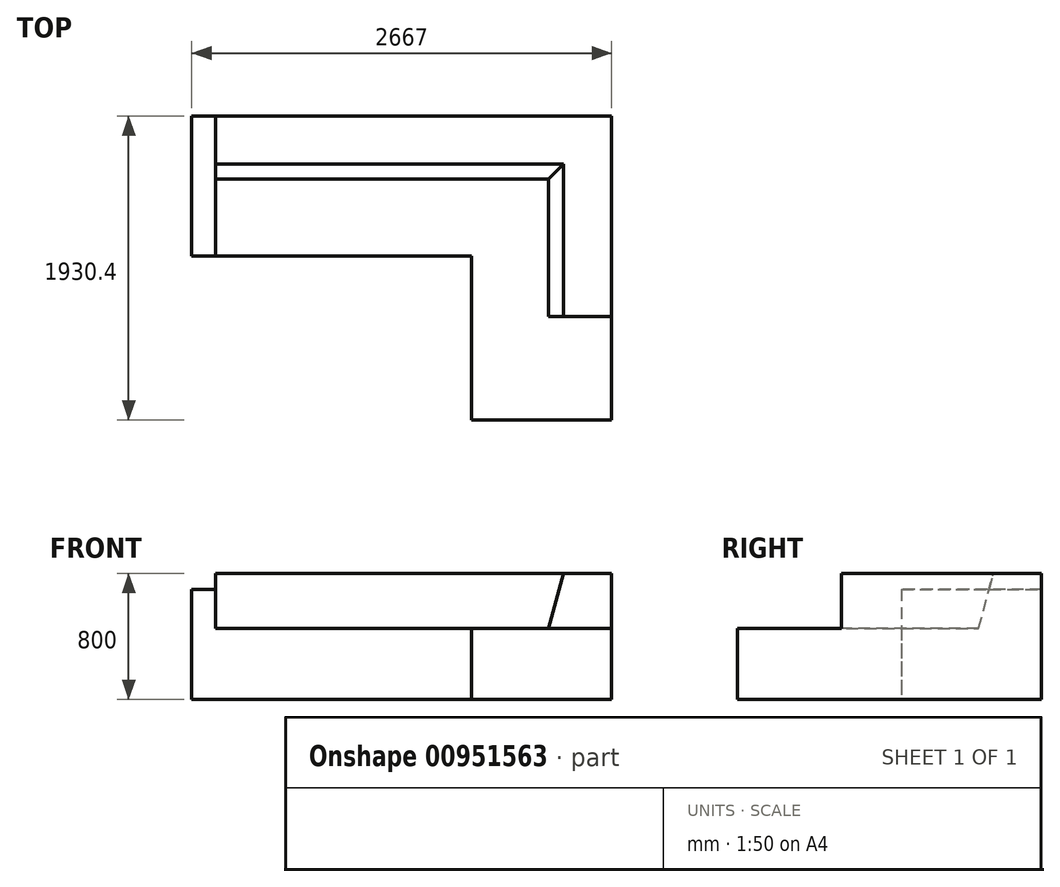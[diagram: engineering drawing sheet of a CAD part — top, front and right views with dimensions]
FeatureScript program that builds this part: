
annotation { "Feature Type Name" : "Feature", "Feature Type Description" : "" }
export const myFeature = defineFeature(function(context is Context, id is Id, definition is map)
    precondition{}
    {
        {
            var Q0;
            Q0=qCreatedBy(makeId("Top.planeOp"),FACE);
            var sketch = newSketch(context, id + "F0", { "sketchPlane" : qUnion([Q0])});
            skLineSegment(sketch, "E0", {"start": v(0, 0) * mm, "end": v(0, 1930.4) * mm});
            skLineSegment(sketch, "E1", {"start": v(0, 1930.4) * mm, "end": v(2667, 1930.4) * mm});
            skLineSegment(sketch, "E2", {"start": v(0, 0) * mm, "end": v(889, 0) * mm});
            skLineSegment(sketch, "E3", {"start": v(2667, 1930.4) * mm, "end": v(2667, 1041.4) * mm});
            skLineSegment(sketch, "E4", {"start": v(889, 0) * mm, "end": v(889, 1041.4) * mm});
            skLineSegment(sketch, "E5", {"start": v(889, 1041.4) * mm, "end": v(2667, 1041.4) * mm});
            skSolve(sketch);
        }
        {
            var Q0;
            Q0=qSketchRegion(id+"F0",true);
            extrude(context, id + "F1", {"entities" : qUnion([Q0]), "depth" : 450 * mm, "offsetDistance" : 25.4 * mm});
        }
        {
            var Q0;
            Q0=makeQuery(id+"F1.opExtrude","CAP_FACE",FACE,{"disambiguationData":[OSD([sQuery(id+"F0.wireOp",EDGE,"E0"),sQuery(id+"F0.wireOp",EDGE,"E1"),sQuery(id+"F0.wireOp",EDGE,"E2"),sQuery(id+"F0.wireOp",EDGE,"E3"),sQuery(id+"F0.wireOp",EDGE,"E4"),sQuery(id+"F0.wireOp",EDGE,"E5")])],"isStart":false});
            var sketch = newSketch(context, id + "F2", { "sketchPlane" : qUnion([Q0])});
            skLineSegment(sketch, "E6.bottom", {"start": v(889, 0) * mm, "end": v(0, 0) * mm});
            skLineSegment(sketch, "E6.top", {"start": v(889, 150) * mm, "end": v(0, 150) * mm});
            skLineSegment(sketch, "E6.left", {"start": v(889, 0) * mm, "end": v(889, 150) * mm});
            skLineSegment(sketch, "E6.right", {"start": v(0, 0) * mm, "end": v(0, 150) * mm});
            skLineSegment(sketch, "E7.bottom", {"start": v(2667, 1041.4) * mm, "end": v(2517, 1041.4) * mm});
            skLineSegment(sketch, "E7.top", {"start": v(2667, 1930.4) * mm, "end": v(2517, 1930.4) * mm});
            skLineSegment(sketch, "E7.left", {"start": v(2667, 1041.4) * mm, "end": v(2667, 1930.4) * mm});
            skLineSegment(sketch, "E7.right", {"start": v(2517, 1041.4) * mm, "end": v(2517, 1930.4) * mm});
            skSolve(sketch);
        }
        {
            var Q0;
            Q0=qSketchRegion(id+"F2",true);
            extrude(context, id + "F3", {"entities" : qUnion([Q0]), "operationType" : NewBodyOperationType.ADD, "depth" : 700 * mm - 450 * mm, "offsetDistance" : 25.4 * mm});
        }
        {
            var Q0;
            Q0=makeQuery(id+"F3.opExtrude","SWEPT_FACE",FACE,{"disambiguationData":[OSD([sQuery(id+"F2.wireOp",EDGE,"E6.top")])]});
            var sketch = newSketch(context, id + "F4", { "sketchPlane" : qUnion([Q0])});
            skLineSegment(sketch, "E8", {"start": v(0, 450) * mm, "end": v(0, 800) * mm});
            skLineSegment(sketch, "E9", {"start": v(0, 800) * mm, "end": v(-306.27, 800) * mm});
            skLineSegment(sketch, "E10", {"start": v(-306.27, 800) * mm, "end": v(-400.05, 450) * mm});
            skLineSegment(sketch, "E11", {"start": v(-400.05, 450) * mm, "end": v(0, 450) * mm});
            skSolve(sketch);
        }
        {
            var Q0;
            Q0=qSketchRegion(id+"F4",true);
            var Q1;
            Q1=makeQuery(id+"F3.boolean.opBoolean","MERGE",FACE,{"derivedFrom":[makeQuery(id+"F1.opExtrude","SWEPT_FACE",FACE,{"disambiguationData":[OSD([sQuery(id+"F0.wireOp",EDGE,"E1")])]}),makeQuery(id+"F3.opExtrude","SWEPT_FACE",FACE,{"disambiguationData":[OSD([sQuery(id+"F2.wireOp",EDGE,"E7.top")])]})]});
            extrude(context, id + "F5", {"entities" : qUnion([Q0]), "operationType" : NewBodyOperationType.ADD, "endBound" : BoundingType.UP_TO_SURFACE, "depth" : 25.4 * mm, "endBoundEntityFace" : qUnion([Q1]), "offsetDistance" : 25.4 * mm});
        }
        {
            var Q0;
            Q0=makeQuery(id+"F3.opExtrude","SWEPT_FACE",FACE,{"disambiguationData":[OSD([sQuery(id+"F2.wireOp",EDGE,"E7.right")])]});
            var sketch = newSketch(context, id + "F6", { "sketchPlane" : qUnion([Q0])});
            skLineSegment(sketch, "E12", {"start": v(-1930.4, 450) * mm, "end": v(-1530.35, 450) * mm});
            skLineSegment(sketch, "E13", {"start": v(-1530.35, 450) * mm, "end": v(-1624.13, 800) * mm});
            skLineSegment(sketch, "E14", {"start": v(-1624.13, 800) * mm, "end": v(-1930.4, 800) * mm});
            skLineSegment(sketch, "E15", {"start": v(-1930.4, 800) * mm, "end": v(-1930.4, 450) * mm});
            skSolve(sketch);
        }
        {
            var Q0;
            Q0=qSketchRegion(id+"F6",true);
            extrude(context, id + "F7", {"entities" : qUnion([Q0]), "operationType" : NewBodyOperationType.ADD, "endBound" : BoundingType.UP_TO_NEXT, "depth" : 25.4 * mm, "offsetDistance" : 25.4 * mm});
        }
        {
            var Q0;
            Q0=makeQuery(id+"F3.boolean.opBoolean","MERGE",FACE,{"derivedFrom":[makeQuery(id+"F1.opExtrude","SWEPT_FACE",FACE,{"disambiguationData":[OSD([sQuery(id+"F0.wireOp",EDGE,"E4")])]}),makeQuery(id+"F3.opExtrude","SWEPT_FACE",FACE,{"disambiguationData":[OSD([sQuery(id+"F2.wireOp",EDGE,"E6.left")])]})]});
            var sketch = newSketch(context, id + "F8", { "sketchPlane" : qUnion([Q0])});
            skLineSegment(sketch, "E16.bottom", {"start": v(658.57, 450) * mm, "end": v(0, 450) * mm});
            skLineSegment(sketch, "E16.top", {"start": v(658.57, 800) * mm, "end": v(0, 800) * mm});
            skLineSegment(sketch, "E16.left", {"start": v(658.57, 450) * mm, "end": v(658.57, 800) * mm});
            skLineSegment(sketch, "E16.right", {"start": v(0, 450) * mm, "end": v(0, 800) * mm});
            skSolve(sketch);
        }
        {
            var Q0;
            Q0=qSketchRegion(id+"F8",true);
            extrude(context, id + "F9", {"entities" : qUnion([Q0]), "operationType" : NewBodyOperationType.REMOVE, "endBound" : BoundingType.THROUGH_ALL, "oppositeDirection" : true, "depth" : 25.4 * mm, "offsetDistance" : 25.4 * mm});
        }
        {
            var Q0;
            Q0=makeQuery(id+"F1.opExtrude","SWEPT_BODY",BODY,{"disambiguationData":[OSD([sQuery(id+"F0.wireOp",EDGE,"E0"),sQuery(id+"F0.wireOp",EDGE,"E1"),sQuery(id+"F0.wireOp",EDGE,"E2"),sQuery(id+"F0.wireOp",EDGE,"E3"),sQuery(id+"F0.wireOp",EDGE,"E4"),sQuery(id+"F0.wireOp",EDGE,"E5")])]});
            var Q1;
            Q1=qCreatedBy(makeId("Right.planeOp"),FACE);
            mirror(context, id + "F10", {"operationType" : NewBodyOperationType.ADD, "entities" : qUnion([Q0]), "mirrorPlane" : qUnion([Q1])});
        }
        {
            var Q0;
            Q0=qCreatedBy(makeId("Right.planeOp"),FACE);
            var sketch = newSketch(context, id + "F11", { "sketchPlane" : qUnion([Q0])});
            skLineSegment(sketch, "E17.bottom", {"start": v(-309.58, -291.68) * mm, "end": v(2775.67, -291.68) * mm});
            skLineSegment(sketch, "E17.top", {"start": v(-309.58, 953.1) * mm, "end": v(2775.67, 953.1) * mm});
            skLineSegment(sketch, "E17.left", {"start": v(-309.58, -291.68) * mm, "end": v(-309.58, 953.1) * mm});
            skLineSegment(sketch, "E17.right", {"start": v(2775.67, -291.68) * mm, "end": v(2775.67, 953.1) * mm});
            skSolve(sketch);
        }
        {
            var Q0;
            Q0 = qSketchRegion(id + "F11", true);
            extrude(context, id + "F12", {"entities" : qUnion([Q0]), "operationType" : NewBodyOperationType.REMOVE, "endBound" : BoundingType.THROUGH_ALL, "depth" : 25.4 * mm, "offsetDistance" : 25.4 * mm});
        }
    });
